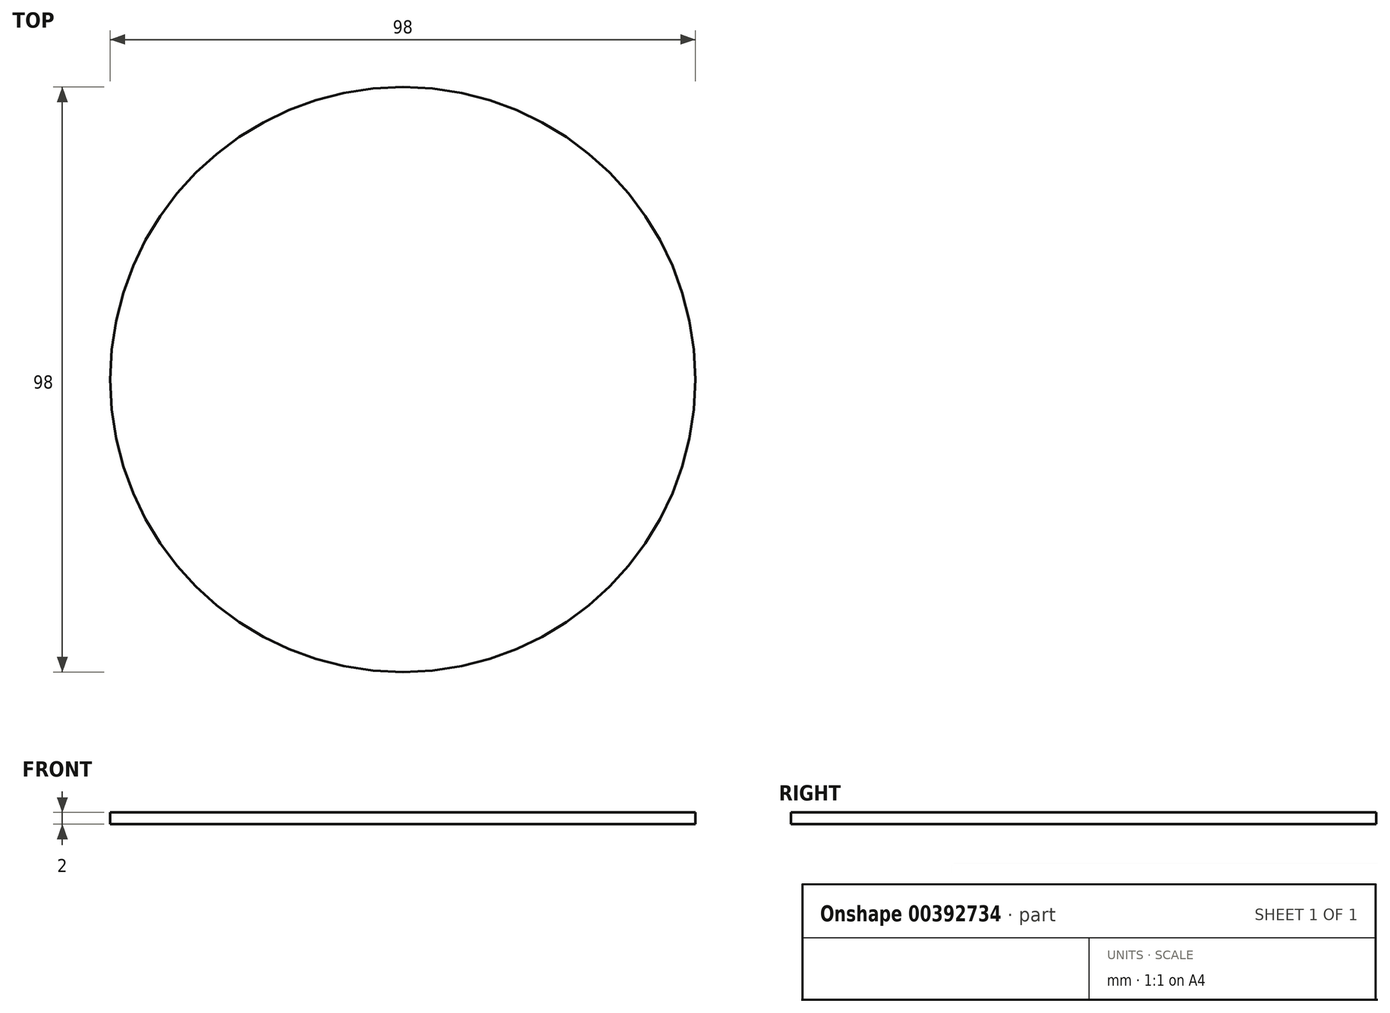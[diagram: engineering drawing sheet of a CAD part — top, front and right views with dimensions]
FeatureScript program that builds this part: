
annotation { "Feature Type Name" : "Feature", "Feature Type Description" : "" }
export const myFeature = defineFeature(function(context is Context, id is Id, definition is map)
    precondition{}
    {
        {
            var Q0;
            Q0=qCreatedBy(makeId("Top.planeOp"),FACE);
            var sketch = newSketch(context, id + "F0", { "sketchPlane" : qUnion([Q0])});
            skCircle(sketch, "E0", {"center": v(0, 0) * mm, "radius": 49 * mm});
            skSolve(sketch);
        }
        {
            var Q0;
            Q0 = qSketchRegion(id + "F0", true);
            extrude(context, id + "F1", {"entities" : qUnion([Q0]), "depth" : 2 * mm});
        }
    });
